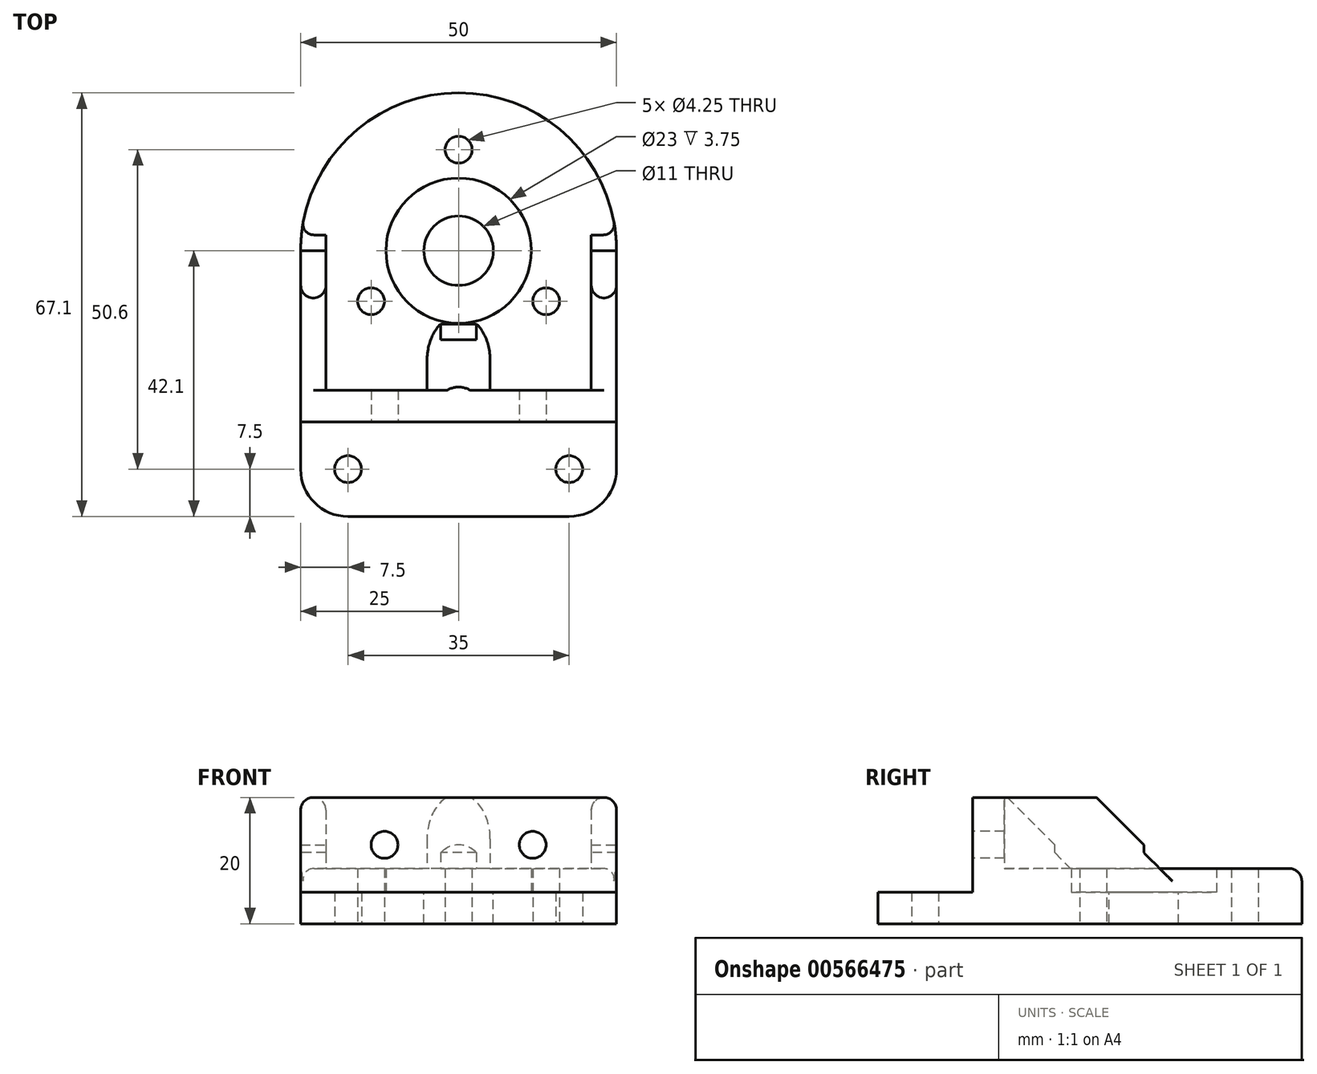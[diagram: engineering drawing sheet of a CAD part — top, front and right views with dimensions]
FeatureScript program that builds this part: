
annotation { "Feature Type Name" : "Feature", "Feature Type Description" : "" }
export const myFeature = defineFeature(function(context is Context, id is Id, definition is map)
    precondition{}
    {
        {
            var Q0;
            Q0=qCreatedBy(makeId("Top.planeOp"),FACE);
            var sketch = newSketch(context, id + "F0", { "sketchPlane" : qUnion([Q0])});
            skCircle(sketch, "E0", {"center": v(0, 0) * mm, "radius": 11.18 * mm, "construction": true});
            skLineSegment(sketch, "E1.bottom", {"start": v(25, -22.1) * mm, "end": v(-25, -22.1) * mm, "construction": true});
            skLineSegment(sketch, "E1.top", {"start": v(25, 22.1) * mm, "end": v(-25, 22.1) * mm, "construction": true});
            skLineSegment(sketch, "E1.left", {"start": v(25, -22.1) * mm, "end": v(25, 0) * mm});
            skLineSegment(sketch, "E1.right", {"start": v(-25, -22.1) * mm, "end": v(-25, 0) * mm});
            skLineSegment(sketch, "E2", {"start": v(-25, -22.1) * mm, "end": v(-25, -27.1) * mm});
            skLineSegment(sketch, "E3", {"start": v(-25, -27.1) * mm, "end": v(25, -27.1) * mm});
            skLineSegment(sketch, "E4", {"start": v(25, -27.1) * mm, "end": v(25, -22.1) * mm});
            skCircle(sketch, "E5", {"center": v(0, 0) * mm, "radius": 5.25 * mm});
            skArc(sketch, "E6", {"start": v(25, 0) * mm, "mid": v(0, 25) * mm, "end": v(-25, 0) * mm});
            skCircle(sketch, "E7", {"center": v(7.5, 0) * mm, "radius": 1.93 * mm, "construction": true});
            skCircle(sketch, "E8.1.0", {"center": v(0, 7.5) * mm, "radius": 1.93 * mm, "construction": true});
            skCircle(sketch, "E8.2.0", {"center": v(-7.5, 0) * mm, "radius": 1.93 * mm, "construction": true});
            skCircle(sketch, "E8.3.0", {"center": v(0, -7.5) * mm, "radius": 1.93 * mm, "construction": true});
            skCircle(sketch, "E9", {"center": v(0, 16) * mm, "radius": 2.12 * mm});
            skCircle(sketch, "E10.1.0", {"center": v(-13.86, -8) * mm, "radius": 2.12 * mm});
            skCircle(sketch, "E10.2.0", {"center": v(13.86, -8) * mm, "radius": 2.12 * mm});
            skSolve(sketch);
        }
        {
            var Q0;
            Q0=qSketchRegion(id+"F0",true);
            extrude(context, id + "F1", {"entities" : qUnion([Q0]), "depth" : 5 * mm});
        }
        {
            var Q0;
            Q0=makeQuery(id+"F1.opExtrude","CAP_FACE",FACE,{"disambiguationData":[OSD([sQuery(id+"F0.wireOp",EDGE,"E1.top"),sQuery(id+"F0.wireOp",EDGE,"E1.left"),sQuery(id+"F0.wireOp",EDGE,"E1.right"),sQuery(id+"F0.wireOp",EDGE,"E2"),sQuery(id+"F0.wireOp",EDGE,"E3"),sQuery(id+"F0.wireOp",EDGE,"E4"),sQuery(id+"F0.wireOp",EDGE,"E5")])],"isStart":false});
            var sketch = newSketch(context, id + "F2", { "sketchPlane" : qUnion([Q0])});
            skLineSegment(sketch, "E11.bottom", {"start": v(25, -27.1) * mm, "end": v(-25, -27.1) * mm});
            skLineSegment(sketch, "E11.top", {"start": v(21, -22.1) * mm, "end": v(5, -22.1) * mm});
            skLineSegment(sketch, "E11.left", {"start": v(25, -27.1) * mm, "end": v(25, -22.1) * mm});
            skLineSegment(sketch, "E11.right", {"start": v(-25, -27.1) * mm, "end": v(-25, -22.1) * mm});
            skPoint(sketch, "E11.middle", {"position": v(0, -24.6) * mm});
            skLineSegment(sketch, "E12", {"start": v(-5, -22.1) * mm, "end": v(-5, -14.1) * mm});
            skLineSegment(sketch, "E13", {"start": v(-5, -14.1) * mm, "end": v(0, -14.1) * mm});
            skLineSegment(sketch, "E14.MirrorCS", {"start": v(5, -14.1) * mm, "end": v(0, -14.1) * mm});
            skLineSegment(sketch, "E15.MirrorCS", {"start": v(5, -22.1) * mm, "end": v(5, -14.1) * mm});
            skLineSegment(sketch, "E16.trimOffspring", {"start": v(-5, -22.1) * mm, "end": v(-21, -22.1) * mm});
            skLineSegment(sketch, "E17", {"start": v(-25, -22.1) * mm, "end": v(-25, 0) * mm});
            skLineSegment(sketch, "E18", {"start": v(-25, 0) * mm, "end": v(-21, 0) * mm});
            skLineSegment(sketch, "E19", {"start": v(-21, 0) * mm, "end": v(-21, -22.1) * mm});
            skLineSegment(sketch, "E20.MirrorCS", {"start": v(21, 0) * mm, "end": v(21, -22.1) * mm});
            skLineSegment(sketch, "E21.MirrorCS", {"start": v(25, 0) * mm, "end": v(21, 0) * mm});
            skLineSegment(sketch, "E22.MirrorCS", {"start": v(25, -22.1) * mm, "end": v(25, 0) * mm});
            skSolve(sketch);
        }
        {
            var Q0;
            Q0=qSketchRegion(id+"F2",true);
            extrude(context, id + "F3", {"entities" : qUnion([Q0]), "operationType" : NewBodyOperationType.ADD, "depth" : 15 * mm});
        }
        {
            var Q0;
            Q0=makeQuery(id+"F3.boolean.opBoolean","MERGE",FACE,{"derivedFrom":[makeQuery(id+"F1.opExtrude","SWEPT_FACE",FACE,{"disambiguationData":[OSD([sQuery(id+"F0.wireOp",EDGE,"E3")])]}),makeQuery(id+"F3.opExtrude","SWEPT_FACE",FACE,{"disambiguationData":[OSD([sQuery(id+"F2.wireOp",EDGE,"E11.bottom")])]})]});
            var sketch = newSketch(context, id + "F4", { "sketchPlane" : qUnion([Q0])});
            skCircle(sketch, "E23", {"center": v(-11.73, 12.5) * mm, "radius": 2.12 * mm});
            skCircle(sketch, "E24.MirrorC", {"center": v(11.72, 12.5) * mm, "radius": 2.12 * mm});
            skSolve(sketch);
        }
        {
            var Q0;
            Q0=qSketchRegion(id+"F4",true);
            extrude(context, id + "F5", {"entities" : qUnion([Q0]), "operationType" : NewBodyOperationType.REMOVE, "oppositeDirection" : true, "depth" : 25 * mm});
        }
        {
            var Q0;
            Q0=qCreatedBy(makeId("Top.planeOp"),FACE);
            var sketch = newSketch(context, id + "F6", { "sketchPlane" : qUnion([Q0])});
            skLineSegment(sketch, "E25.bottom", {"start": v(25, -27.1) * mm, "end": v(-25, -27.1) * mm});
            skLineSegment(sketch, "E25.top", {"start": v(25, -42.1) * mm, "end": v(-25, -42.1) * mm});
            skLineSegment(sketch, "E25.left", {"start": v(25, -27.1) * mm, "end": v(25, -42.1) * mm});
            skLineSegment(sketch, "E25.right", {"start": v(-25, -27.1) * mm, "end": v(-25, -42.1) * mm});
            skPoint(sketch, "E25.middle", {"position": v(0, -34.6) * mm});
            skCircle(sketch, "E26", {"center": v(-17.5, -34.6) * mm, "radius": 2.12 * mm});
            skCircle(sketch, "E27.MirrorC", {"center": v(17.5, -34.6) * mm, "radius": 2.12 * mm});
            skSolve(sketch);
        }
        {
            var Q0;
            Q0=qSketchRegion(id+"F6",true);
            extrude(context, id + "F7", {"entities" : qUnion([Q0]), "operationType" : NewBodyOperationType.ADD, "depth" : 5 * mm});
        }
        {
            var Q0;
            Q0=makeQuery(id+"F7.opExtrude","SWEPT_EDGE",EDGE,{"disambiguationData":[OSD([sQuery(id+"F6.wireOp",EDGE,"E25.top"),sQuery(id+"F6.wireOp",EDGE,"E25.right")])]});
            var Q1;
            Q1=makeQuery(id+"F7.opExtrude","SWEPT_EDGE",EDGE,{"disambiguationData":[OSD([sQuery(id+"F6.wireOp",EDGE,"E25.top"),sQuery(id+"F6.wireOp",EDGE,"E25.left")])]});
            fillet(context, id + "F8", {"entities" : qUnion([Q0, Q1]), "radius" : 7.5 * mm, "tangentPropagation" : true, "allowEdgeOverflow" : false});
        }
        {
            var Q0;
            Q0=makeQuery(id+"F3.opExtrude","CAP_EDGE",EDGE,{"disambiguationData":[OSD([sQuery(id+"F2.wireOp",EDGE,"E13"),sQuery(id+"F2.wireOp",EDGE,"E14.MirrorCS")])],"isStart":false});
            var Q1;
            Q1=makeQuery(id+"F3.opExtrude","CAP_EDGE",EDGE,{"disambiguationData":[OSD([sQuery(id+"F2.wireOp",EDGE,"E18")])],"isStart":false});
            var Q2;
            Q2=makeQuery(id+"F3.opExtrude","CAP_EDGE",EDGE,{"disambiguationData":[OSD([sQuery(id+"F2.wireOp",EDGE,"E21.MirrorCS")])],"isStart":false});
            chamfer(context, id + "F9", {"entities" : qUnion([Q0, Q1, Q2]), "width" : 7.5 * mm, "tangentPropagation" : true});
        }
        {
            var Q0;
            Q0=makeQuery(id+"F1.opExtrude","CAP_FACE",FACE,{"disambiguationData":[OSD([sQuery(id+"F0.wireOp",EDGE,"E1.left"),sQuery(id+"F0.wireOp",EDGE,"E1.right"),sQuery(id+"F0.wireOp",EDGE,"E2"),sQuery(id+"F0.wireOp",EDGE,"E3"),sQuery(id+"F0.wireOp",EDGE,"E4"),sQuery(id+"F0.wireOp",EDGE,"E5"),sQuery(id+"F0.wireOp",EDGE,"E6"),sQuery(id+"F0.wireOp",EDGE,"E7"),sQuery(id+"F0.wireOp",EDGE,"E8.1.0"),sQuery(id+"F0.wireOp",EDGE,"E8.2.0"),sQuery(id+"F0.wireOp",EDGE,"E8.3.0")])],"isStart":false});
            var sketch = newSketch(context, id + "F10", { "sketchPlane" : qUnion([Q0])});
            skCircle(sketch, "E28", {"center": v(0, 0) * mm, "radius": 11.5 * mm});
            skArc(sketch, "E29", {"start": v(25, 0) * mm, "mid": v(0, 25) * mm, "end": v(-25, 0) * mm});
            skLineSegment(sketch, "E30", {"start": v(-25, 0) * mm, "end": v(-25, -22.1) * mm});
            skLineSegment(sketch, "E31", {"start": v(25, -22.1) * mm, "end": v(25, 0) * mm});
            skLineSegment(sketch, "E32", {"start": v(-25, -22.1) * mm, "end": v(25, -22.1) * mm});
            skCircle(sketch, "E33", {"center": v(13.86, -8) * mm, "radius": 2.12 * mm});
            skCircle(sketch, "E34.1.0", {"center": v(0, 16) * mm, "radius": 2.12 * mm});
            skCircle(sketch, "E34.2.0", {"center": v(-13.86, -8) * mm, "radius": 2.12 * mm});
            skSolve(sketch);
        }
        {
            var Q0;
            Q0=qSketchRegion(id+"F10",true);
            extrude(context, id + "F11", {"entities" : qUnion([Q0]), "operationType" : NewBodyOperationType.ADD, "depth" : 3.75 * mm});
        }
        {
            var Q0;
            Q0=makeQuery(id+"F11.boolean.opBoolean","INTERSECT",EDGE,{"derivedFrom":[makeQuery(id+"F3.opExtrude","SWEPT_FACE",FACE,{"disambiguationData":[OSD([sQuery(id+"F2.wireOp",EDGE,"E13"),sQuery(id+"F2.wireOp",EDGE,"E14.MirrorCS")])]}),makeQuery(id+"F11.opExtrude","CAP_FACE",FACE,{"disambiguationData":[OSD([sQuery(id+"F10.wireOp",EDGE,"E28"),sQuery(id+"F10.wireOp",EDGE,"E29"),sQuery(id+"F10.wireOp",EDGE,"E30"),sQuery(id+"F10.wireOp",EDGE,"KMwbHocN-jLKF-1fT8-stF3-EZ2oOHbS1cSO"),sQuery(id+"F10.wireOp",EDGE,"Onsy7AXm-IlgJ-wlJu-APFR-eMNSHrUauErb"),sQuery(id+"F10.wireOp",EDGE,"E31")])],"isStart":false})]});
            var Q1;
            Q1=makeQuery(id+"F11.boolean.opBoolean","INTERSECT",EDGE,{"derivedFrom":[makeQuery(id+"F3.opExtrude","SWEPT_FACE",FACE,{"disambiguationData":[OSD([sQuery(id+"F2.wireOp",EDGE,"E18")])]}),makeQuery(id+"F11.opExtrude","CAP_FACE",FACE,{"disambiguationData":[OSD([sQuery(id+"F10.wireOp",EDGE,"E28"),sQuery(id+"F10.wireOp",EDGE,"E29"),sQuery(id+"F10.wireOp",EDGE,"E30"),sQuery(id+"F10.wireOp",EDGE,"KMwbHocN-jLKF-1fT8-stF3-EZ2oOHbS1cSO"),sQuery(id+"F10.wireOp",EDGE,"Onsy7AXm-IlgJ-wlJu-APFR-eMNSHrUauErb"),sQuery(id+"F10.wireOp",EDGE,"E31")])],"isStart":false})]});
            var Q2;
            Q2=makeQuery(id+"F11.boolean.opBoolean","INTERSECT",EDGE,{"derivedFrom":[makeQuery(id+"F3.opExtrude","SWEPT_FACE",FACE,{"disambiguationData":[OSD([sQuery(id+"F2.wireOp",EDGE,"E21.MirrorCS")])]}),makeQuery(id+"F11.opExtrude","CAP_FACE",FACE,{"disambiguationData":[OSD([sQuery(id+"F10.wireOp",EDGE,"E29"),sQuery(id+"F10.wireOp",EDGE,"E30"),sQuery(id+"F10.wireOp",EDGE,"E31"),sQuery(id+"F10.wireOp",EDGE,"E32"),sQuery(id+"F10.wireOp",EDGE,"2727002f-cbe3-4c88-9281-592464c8ef14.0"),sQuery(id+"F10.wireOp",EDGE,"2727002f-cbe3-4c88-9281-592464c8ef14.1"),sQuery(id+"F10.wireOp",EDGE,"2727002f-cbe3-4c88-9281-592464c8ef14.2"),sQuery(id+"F10.wireOp",EDGE,"2727002f-cbe3-4c88-9281-592464c8ef14.3"),sQuery(id+"F10.wireOp",EDGE,"2727002f-cbe3-4c88-9281-592464c8ef14.4"),sQuery(id+"F10.wireOp",EDGE,"2727002f-cbe3-4c88-9281-592464c8ef14.5"),sQuery(id+"F10.wireOp",EDGE,"b888d105-8f6f-4c9c-b178-63c6b7cefb370.MirrorCS"),sQuery(id+"F10.wireOp",EDGE,"b888d105-8f6f-4c9c-b178-63c6b7cefb371.MirrorCS"),sQuery(id+"F10.wireOp",EDGE,"b888d105-8f6f-4c9c-b178-63c6b7cefb372.MirrorCS"),sQuery(id+"F10.wireOp",EDGE,"b888d105-8f6f-4c9c-b178-63c6b7cefb373.MirrorCS"),sQuery(id+"F10.wireOp",EDGE,"b888d105-8f6f-4c9c-b178-63c6b7cefb374.MirrorCS"),sQuery(id+"F10.wireOp",EDGE,"E28"),sQuery(id+"F10.wireOp",EDGE,"b888d105-8f6f-4c9c-b178-63c6b7cefb376.MirrorCS"),sQuery(id+"F10.wireOp",EDGE,"fa7a15cb-9f2a-4baf-ae83-e6cc382a87b4.0"),sQuery(id+"F10.wireOp",EDGE,"fa7a15cb-9f2a-4baf-ae83-e6cc382a87b4.1"),sQuery(id+"F10.wireOp",EDGE,"fa7a15cb-9f2a-4baf-ae83-e6cc382a87b4.2"),sQuery(id+"F10.wireOp",EDGE,"fa7a15cb-9f2a-4baf-ae83-e6cc382a87b4.3"),sQuery(id+"F10.wireOp",EDGE,"fa7a15cb-9f2a-4baf-ae83-e6cc382a87b4.4"),sQuery(id+"F10.wireOp",EDGE,"fa7a15cb-9f2a-4baf-ae83-e6cc382a87b4.5")])],"isStart":false})]});
            chamfer(context, id + "F12", {"entities" : qUnion([Q0, Q1, Q2]), "width" : 2.5 * mm, "tangentPropagation" : true});
        }
        {
            var Q0;
            Q0=makeQuery(id+"F9.opChamfer","BLEND_EDGE",EDGE,{"blendedFrom":[makeQuery(id+"F3.opExtrude","CAP_EDGE",EDGE,{"disambiguationData":[OSD([sQuery(id+"F2.wireOp",EDGE,"E13"),sQuery(id+"F2.wireOp",EDGE,"E14.MirrorCS")])],"isStart":false}),makeQuery(id+"F3.opExtrude","SWEPT_FACE",FACE,{"disambiguationData":[OSD([sQuery(id+"F2.wireOp",EDGE,"E15.MirrorCS")])]})],"blendedInto":[makeQuery(id+"F3.opExtrude","SWEPT_FACE",FACE,{"disambiguationData":[OSD([sQuery(id+"F2.wireOp",EDGE,"E15.MirrorCS")])]})]});
            var Q1;
            Q1=makeQuery(id+"F9.opChamfer","BLEND_EDGE",EDGE,{"blendedFrom":[makeQuery(id+"F3.opExtrude","CAP_EDGE",EDGE,{"disambiguationData":[OSD([sQuery(id+"F2.wireOp",EDGE,"E13"),sQuery(id+"F2.wireOp",EDGE,"E14.MirrorCS")])],"isStart":false}),makeQuery(id+"F3.opExtrude","SWEPT_FACE",FACE,{"disambiguationData":[OSD([sQuery(id+"F2.wireOp",EDGE,"E12")])]})],"blendedInto":[makeQuery(id+"F3.opExtrude","SWEPT_FACE",FACE,{"disambiguationData":[OSD([sQuery(id+"F2.wireOp",EDGE,"E12")])]})]});
            fillet(context, id + "F13", {"entities" : qUnion([Q0, Q1]), "radius" : 5 * mm, "tangentPropagation" : true, "allowEdgeOverflow" : false});
        }
        {
            var Q0;
            Q0=makeQuery(id+"F3.opExtrude","CAP_EDGE",EDGE,{"disambiguationData":[OSD([sQuery(id+"F2.wireOp",EDGE,"E20.MirrorCS")])],"isStart":false});
            var Q1;
            Q1=makeQuery(id+"F3.opExtrude","CAP_EDGE",EDGE,{"disambiguationData":[OSD([sQuery(id+"F2.wireOp",EDGE,"E11.left"),sQuery(id+"F2.wireOp",EDGE,"E22.MirrorCS")])],"isStart":false});
            var Q2;
            Q2=makeQuery(id+"F3.opExtrude","CAP_EDGE",EDGE,{"disambiguationData":[OSD([sQuery(id+"F2.wireOp",EDGE,"E19")])],"isStart":false});
            var Q3;
            Q3=makeQuery(id+"F3.opExtrude","CAP_EDGE",EDGE,{"disambiguationData":[OSD([sQuery(id+"F2.wireOp",EDGE,"E11.right"),sQuery(id+"F2.wireOp",EDGE,"E17")])],"isStart":false});
            var Q4;
            Q4=makeQuery(id+"F11.opExtrude","CAP_EDGE",EDGE,{"disambiguationData":[OSD([sQuery(id+"F10.wireOp",EDGE,"E29")])],"isStart":false});
            fillet(context, id + "F14", {"entities" : qUnion([Q0, Q1, Q2, Q3, Q4]), "radius" : 2 * mm, "tangentPropagation" : true, "allowEdgeOverflow" : false});
        }
        {
            var Q0;
            Q0=makeQuery(id+"F1.opExtrude","CAP_FACE",FACE,{"disambiguationData":[OSD([sQuery(id+"F0.wireOp",EDGE,"E1.left"),sQuery(id+"F0.wireOp",EDGE,"E1.right"),sQuery(id+"F0.wireOp",EDGE,"E2"),sQuery(id+"F0.wireOp",EDGE,"E3"),sQuery(id+"F0.wireOp",EDGE,"E4"),sQuery(id+"F0.wireOp",EDGE,"E5"),sQuery(id+"F0.wireOp",EDGE,"E6"),sQuery(id+"F0.wireOp",EDGE,"E7"),sQuery(id+"F0.wireOp",EDGE,"E8.1.0"),sQuery(id+"F0.wireOp",EDGE,"E8.2.0"),sQuery(id+"F0.wireOp",EDGE,"E8.3.0")])],"isStart":false});
            var sketch = newSketch(context, id + "F15", { "sketchPlane" : qUnion([Q0])});
            skCircle(sketch, "E35", {"center": v(0, 0) * mm, "radius": 5.5 * mm});
            skSolve(sketch);
        }
        {
            var Q0;
            Q0=qSketchRegion(id+"F15",true);
            extrude(context, id + "F16", {"entities" : qUnion([Q0]), "operationType" : NewBodyOperationType.REMOVE, "oppositeDirection" : true, "depth" : 25 * mm});
        }
    });
